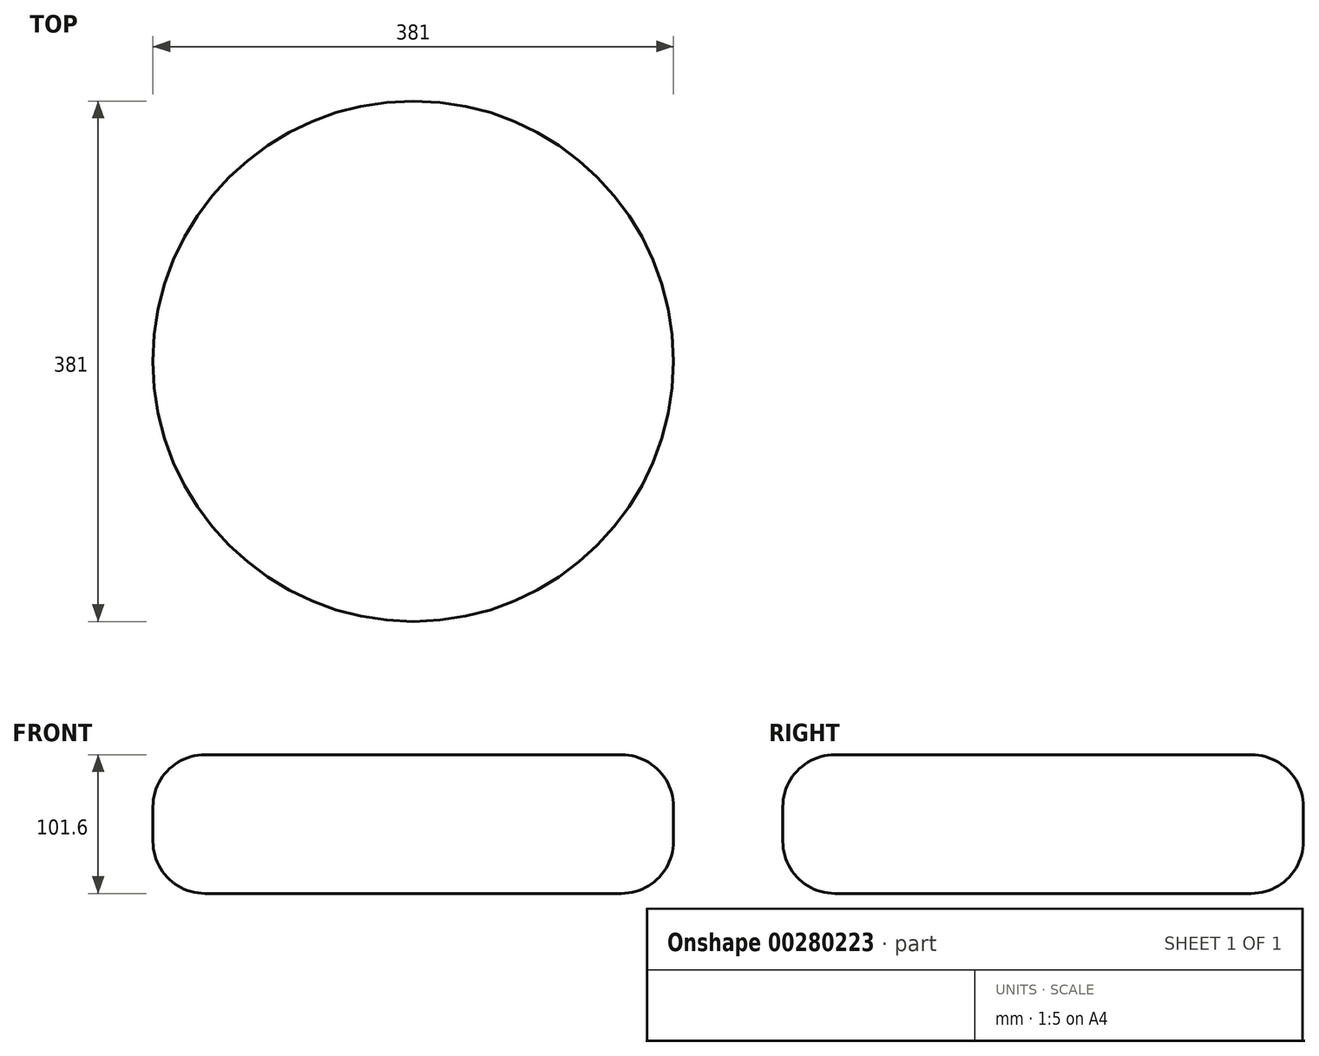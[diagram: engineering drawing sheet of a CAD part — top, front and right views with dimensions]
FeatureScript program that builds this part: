
annotation { "Feature Type Name" : "Feature", "Feature Type Description" : "" }
export const myFeature = defineFeature(function(context is Context, id is Id, definition is map)
    precondition{}
    {
        {
            var Q0;
            Q0=qCreatedBy(makeId("Top.planeOp"),FACE);
            var sketch = newSketch(context, id + "F0", { "sketchPlane" : qUnion([Q0])});
            skCircle(sketch, "E0", {"center": v(0, 0) * mm, "radius": 190.5 * mm});
            skSolve(sketch);
        }
        {
            var Q0;
            Q0 = qSketchRegion(id + "F0", true);
            extrude(context, id + "F1", {"entities" : qUnion([Q0]), "depth" : 101.6 * mm});
        }
        {
            var Q0;
            Q0=makeQuery(id+"F1.opExtrude","CAP_FACE",FACE,{"disambiguationData":[OSD([sQuery(id+"F0.wireOp",EDGE,"E0")])],"isStart":false});
            fillet(context, id + "F2", {"entities" : qUnion([Q0]), "radius" : 38.1 * mm, "tangentPropagation" : true, "allowEdgeOverflow" : false});
        }
        {
            var Q0;
            Q0=makeQuery(id+"F1.opExtrude","CAP_EDGE",EDGE,{"disambiguationData":[OSD([sQuery(id+"F0.wireOp",EDGE,"E0")])],"isStart":true});
            fillet(context, id + "F3", {"entities" : qUnion([Q0]), "radius" : 38.1 * mm, "tangentPropagation" : true, "allowEdgeOverflow" : false});
        }
        {
            var Q0;
            Q0=qCreatedBy(makeId("Front.planeOp"),FACE);
            cPlane(context, id + "F4", {"entities" : qUnion([Q0]), "cplaneType" : CPlaneType.OFFSET, "offset" : 114.3 * mm, "width" : 152.4 * mm, "height" : 152.4 * mm});
        }
        {
            var Q0;
            Q0=qCreatedBy(id+"F4.planeOp",FACE);
            var sketch = newSketch(context, id + "F5", { "sketchPlane" : qUnion([Q0])});
            skPoint(sketch, "E1.middle", {"position": v(0, 0) * mm});
            skLineSegment(sketch, "E2.bottom", {"start": v(-120.36, 126.53) * mm, "end": v(120.36, 126.53) * mm, "construction": true});
            skLineSegment(sketch, "E2.top", {"start": v(-120.36, -126.53) * mm, "end": v(120.36, -126.53) * mm, "construction": true});
            skLineSegment(sketch, "E2.left", {"start": v(-120.36, 126.53) * mm, "end": v(-120.36, -126.53) * mm, "construction": true});
            skLineSegment(sketch, "E2.right", {"start": v(120.36, 126.53) * mm, "end": v(120.36, -126.53) * mm, "construction": true});
            skSolve(sketch);
        }
        {
            var Q0;
            Q0=sQuery(id+"F5.wireOp",EDGE,"E2.bottom");
            cPlane(context, id + "F6", {"entities" : qUnion([Q0]), "cplaneType" : CPlaneType.LINE_ANGLE, "offset" : 25.4 * mm, "angle" : 11 * degree, "oppositeDirection" : true, "width" : 152.4 * mm, "height" : 152.4 * mm});
        }
        {
            var Q0;
            Q0=qCreatedBy(makeId("Front.planeOp"),FACE);
            cPlane(context, id + "F7", {"entities" : qUnion([Q0]), "cplaneType" : CPlaneType.OFFSET, "offset" : 114.3 * mm, "oppositeDirection" : true, "width" : 152.4 * mm, "height" : 152.4 * mm});
        }
        {
            var Q0;
            Q0=qCreatedBy(id+"F7.planeOp",FACE);
            var sketch = newSketch(context, id + "F8", { "sketchPlane" : qUnion([Q0])});
            skLineSegment(sketch, "E3.bottom", {"start": v(234.82, 265.1) * mm, "end": v(-150.03, 265.1) * mm, "construction": true});
            skLineSegment(sketch, "E3.top", {"start": v(234.82, -300.83) * mm, "end": v(-150.03, -300.83) * mm, "construction": true});
            skLineSegment(sketch, "E3.left", {"start": v(234.82, 265.1) * mm, "end": v(234.82, -300.83) * mm, "construction": true});
            skLineSegment(sketch, "E3.right", {"start": v(-150.03, 265.1) * mm, "end": v(-150.03, -300.83) * mm, "construction": true});
            skPoint(sketch, "E3.middle", {"position": v(42.4, -17.86) * mm});
            skSolve(sketch);
        }
    });
